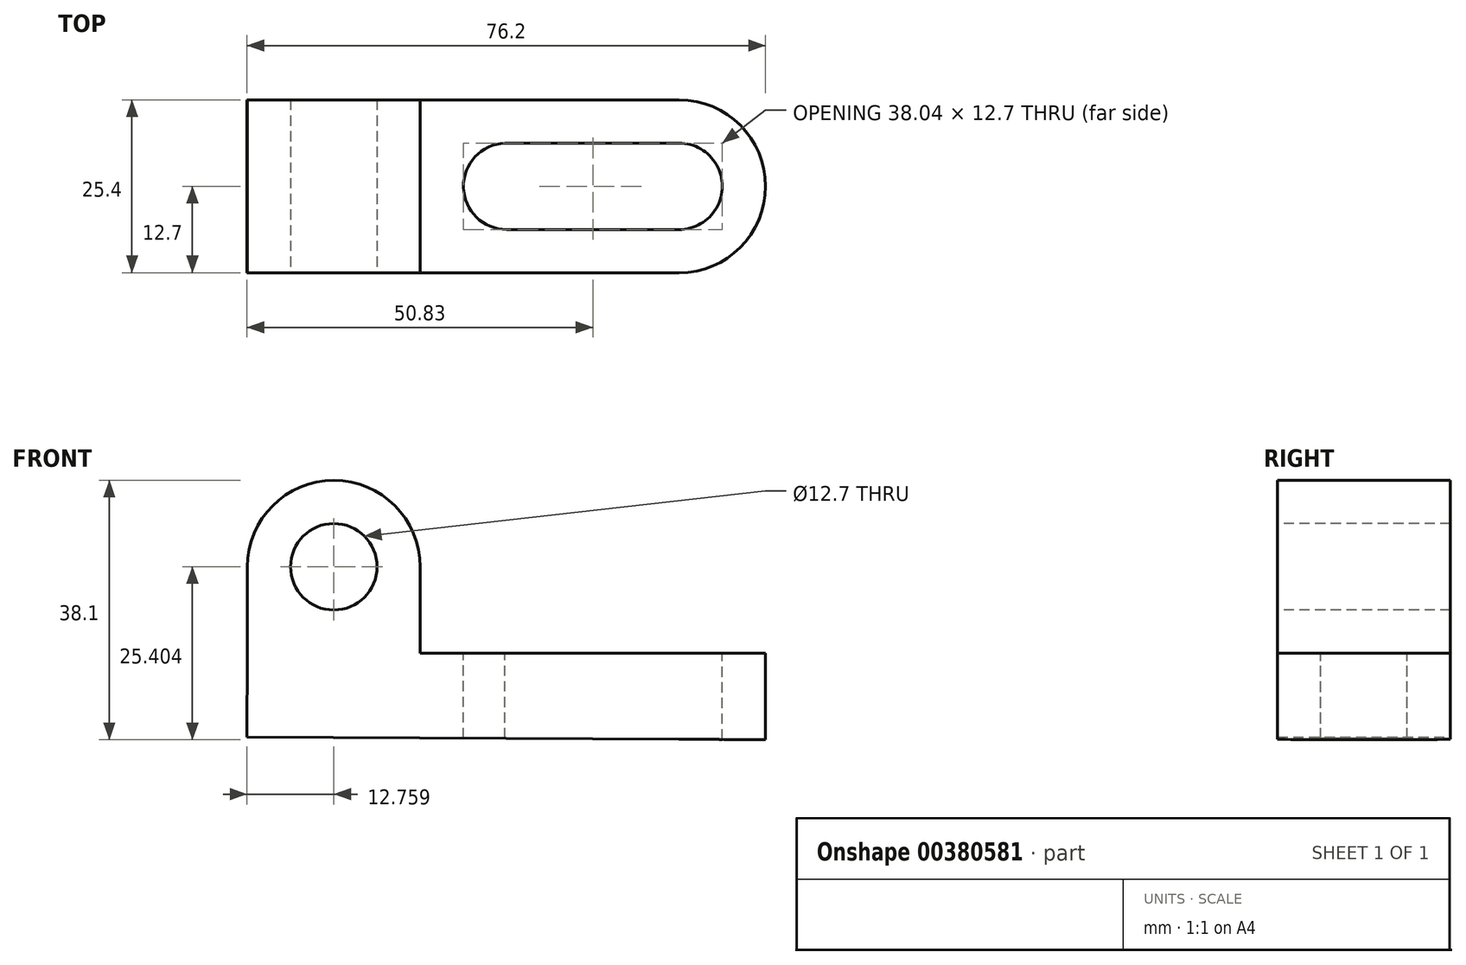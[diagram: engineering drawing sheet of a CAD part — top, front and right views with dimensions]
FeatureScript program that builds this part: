
annotation { "Feature Type Name" : "Feature", "Feature Type Description" : "" }
export const myFeature = defineFeature(function(context is Context, id is Id, definition is map)
    precondition{}
    {
        {
            var Q0;
            Q0=qCreatedBy(makeId("Front.planeOp"),FACE);
            var sketch = newSketch(context, id + "F0", { "sketchPlane" : qUnion([Q0])});
            skLineSegment(sketch, "E0", {"start": v(-29.98, 34.37) * mm, "end": v(-30.04, 22.04) * mm});
            skLineSegment(sketch, "E1", {"start": v(-30.04, 22.04) * mm, "end": v(46.16, 21.67) * mm});
            skLineSegment(sketch, "E2", {"start": v(-4.58, 34.37) * mm, "end": v(46.16, 34.37) * mm});
            skLineSegment(sketch, "E3", {"start": v(46.16, 34.37) * mm, "end": v(46.16, 21.67) * mm});
            skLineSegment(sketch, "E4", {"start": v(-29.98, 34.37) * mm, "end": v(-29.98, 47.07) * mm});
            skLineSegment(sketch, "E5", {"start": v(-4.58, 34.37) * mm, "end": v(-4.58, 47.07) * mm});
            skArc(sketch, "E6", {"start": v(-4.58, 47.07) * mm, "mid": v(-17.28, 59.77) * mm, "end": v(-29.98, 47.07) * mm});
            skSolve(sketch);
        }
        {
            var Q0;
            Q0 = qSketchRegion(id + "F0", true);
            extrude(context, id + "F1", {"entities" : qUnion([Q0]), "depth" : 25.4 * mm});
        }
        {
            var Q0;
            Q0=makeQuery(id+"F1.opExtrude","CAP_FACE",FACE,{"disambiguationData":[OSD([sQuery(id+"F0.wireOp",EDGE,"E0"),sQuery(id+"F0.wireOp",EDGE,"E1"),sQuery(id+"F0.wireOp",EDGE,"E2"),sQuery(id+"F0.wireOp",EDGE,"E3"),sQuery(id+"F0.wireOp",EDGE,"E4"),sQuery(id+"F0.wireOp",EDGE,"E5"),sQuery(id+"F0.wireOp",EDGE,"E6")])],"isStart":false});
            var sketch = newSketch(context, id + "F2", { "sketchPlane" : qUnion([Q0])});
            skCircle(sketch, "E7", {"center": v(-17.28, 47.07) * mm, "radius": 6.35 * mm});
            skSolve(sketch);
        }
        {
            var Q0;
            Q0=makeQuery(id+"F2.imprint","IMPRINT",FACE,{"disambiguationData":[TD([[makeQuery(id+"F2.imprint","IMPRINT",EDGE,{"derivedFrom":sQuery(id+"F2.wireOp",EDGE,"E7")}),1.0]])]});
            extrude(context, id + "F3", {"entities" : qUnion([Q0]), "operationType" : NewBodyOperationType.REMOVE, "oppositeDirection" : true, "depth" : 25.4 * mm});
        }
        {
            var Q0;
            Q0=makeQuery(id+"F1.opExtrude","SWEPT_FACE",FACE,{"disambiguationData":[OSD([sQuery(id+"F0.wireOp",EDGE,"E2")])]});
            var sketch = newSketch(context, id + "F4", { "sketchPlane" : qUnion([Q0])});
            skCircle(sketch, "E8", {"center": v(33.46, -12.7) * mm, "radius": 12.7 * mm});
            skSolve(sketch);
        }
        {
            var Q0;
            {var subQ0=sQuery(id+"F4.wireOp",EDGE,"E8");var subQ1=sQuery(id+"F0.wireOp",EDGE,"E2");var subQ2=makeQuery(id+"F1.opExtrude","CAP_EDGE",EDGE,{"disambiguationData":[OSD([subQ1])],"isStart":true});var subQ3=makeQuery(id+"F4.imprint","INTERSECT",VERTEX,{"derivedFrom":[subQ2,subQ0]});Q0=makeQuery(id+"F4.imprint","IMPRINT",FACE,{"disambiguationData":[TD([[makeQuery(id+"F4.imprint","IMPRINT",EDGE,{"disambiguationData":[TD([[subQ3,1.0]])],"derivedFrom":subQ0}),-1.0]])]});}
            var Q1;
            {var subQ0=sQuery(id+"F4.wireOp",EDGE,"E8");var subQ1=sQuery(id+"F0.wireOp",EDGE,"E2");var subQ4=makeQuery(id+"F1.opExtrude","CAP_EDGE",EDGE,{"disambiguationData":[OSD([subQ1])],"isStart":false});var subQ5=makeQuery(id+"F4.imprint","INTERSECT",VERTEX,{"derivedFrom":[subQ4,subQ0]});Q1=makeQuery(id+"F4.imprint","IMPRINT",FACE,{"disambiguationData":[TD([[makeQuery(id+"F4.imprint","IMPRINT",EDGE,{"disambiguationData":[TD([[subQ5,-1.0]])],"derivedFrom":subQ0}),-1.0]])]});}
            extrude(context, id + "F5", {"entities" : qUnion([Q0, Q1]), "operationType" : NewBodyOperationType.REMOVE, "oppositeDirection" : true, "depth" : 12.7 * mm});
        }
        {
            var Q0;
            Q0=makeQuery(id+"F1.opExtrude","SWEPT_FACE",FACE,{"disambiguationData":[OSD([sQuery(id+"F0.wireOp",EDGE,"E2")])]});
            var sketch = newSketch(context, id + "F6", { "sketchPlane" : qUnion([Q0])});
            skCircle(sketch, "E9", {"center": v(8.12, -12.7) * mm, "radius": 6.35 * mm});
            skCircle(sketch, "E10", {"center": v(33.46, -12.7) * mm, "radius": 6.35 * mm});
            skLineSegment(sketch, "E11", {"start": v(8.12, -19.05) * mm, "end": v(33.46, -19.05) * mm});
            skLineSegment(sketch, "E12", {"start": v(7.84, -6.36) * mm, "end": v(33.46, -6.35) * mm});
            skSolve(sketch);
        }
        {
            var Q0;
            {var subQ0=sQuery(id+"F6.wireOp",EDGE,"E9");var subQ1=makeQuery(id+"F6.imprint","INTERSECT",VERTEX,{"derivedFrom":[subQ0,sQuery(id+"F6.wireOp",EDGE,"E11")]});Q0=makeQuery(id+"F6.imprint","IMPRINT",FACE,{"disambiguationData":[TD([[makeQuery(id+"F6.imprint","IMPRINT",EDGE,{"disambiguationData":[TD([[subQ1,1.0]])],"derivedFrom":subQ0}),1.0]])]});}
            var Q1;
            {var subQ0=sQuery(id+"F6.wireOp",EDGE,"E11");Q1=makeQuery(id+"F6.imprint","IMPRINT",FACE,{"disambiguationData":[TD([[makeQuery(id+"F6.imprint","IMPRINT",EDGE,{"derivedFrom":subQ0}),1.0]])]});}
            var Q2;
            {var subQ0=sQuery(id+"F6.wireOp",EDGE,"E10");var subQ1=makeQuery(id+"F6.imprint","INTERSECT",VERTEX,{"derivedFrom":[subQ0,sQuery(id+"F6.wireOp",EDGE,"E11")]});Q2=makeQuery(id+"F6.imprint","IMPRINT",FACE,{"disambiguationData":[TD([[makeQuery(id+"F6.imprint","IMPRINT",EDGE,{"disambiguationData":[TD([[subQ1,1.0]])],"derivedFrom":subQ0}),1.0]])]});}
            extrude(context, id + "F7", {"entities" : qUnion([Q0, Q1, Q2]), "operationType" : NewBodyOperationType.REMOVE, "oppositeDirection" : true, "depth" : 25.4 * mm});
        }
    });
